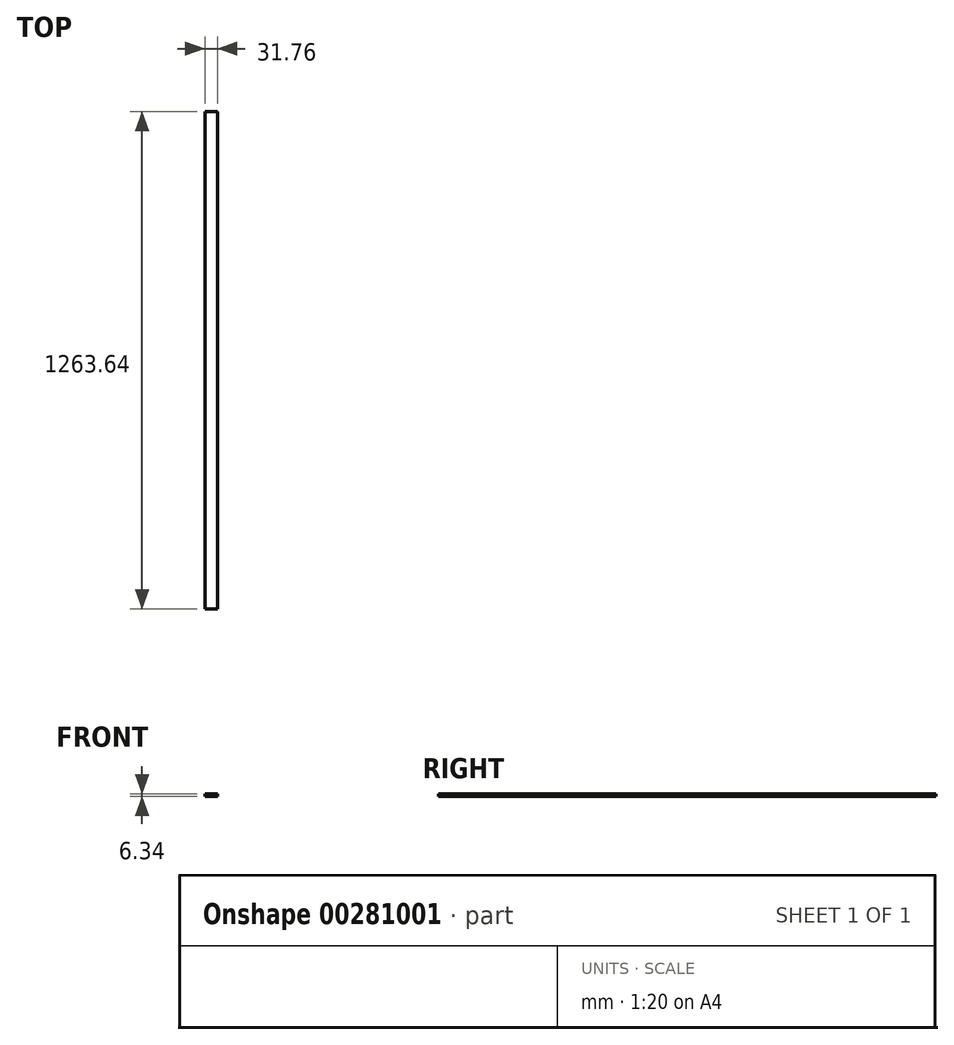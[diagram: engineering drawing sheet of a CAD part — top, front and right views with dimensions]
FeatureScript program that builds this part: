
annotation { "Feature Type Name" : "Feature", "Feature Type Description" : "" }
export const myFeature = defineFeature(function(context is Context, id is Id, definition is map)
    precondition{}
    {
        {
            var Q0;
            Q0=qCreatedBy(makeId("Front.planeOp"),FACE);
            var sketch = newSketch(context, id + "F0", { "sketchPlane" : qUnion([Q0])});
            skLineSegment(sketch, "E0.bottom", {"start": v(15.88, -3.17) * mm, "end": v(-15.88, -3.18) * mm});
            skLineSegment(sketch, "E0.top", {"start": v(15.88, 3.18) * mm, "end": v(-15.88, 3.17) * mm});
            skLineSegment(sketch, "E0.left", {"start": v(15.88, -3.17) * mm, "end": v(15.88, 3.18) * mm});
            skLineSegment(sketch, "E0.right", {"start": v(-15.88, -3.18) * mm, "end": v(-15.88, 3.17) * mm});
            skPoint(sketch, "E0.middle", {"position": v(0, 0) * mm});
            skSolve(sketch);
        }
        {
            var Q0;
            Q0 = qSketchRegion(id + "F0", true);
            extrude(context, id + "F1", {"entities" : qUnion([Q0]), "endBound" : BoundingType.SYMMETRIC, "depth" : 1263.65 * mm});
        }
    });
